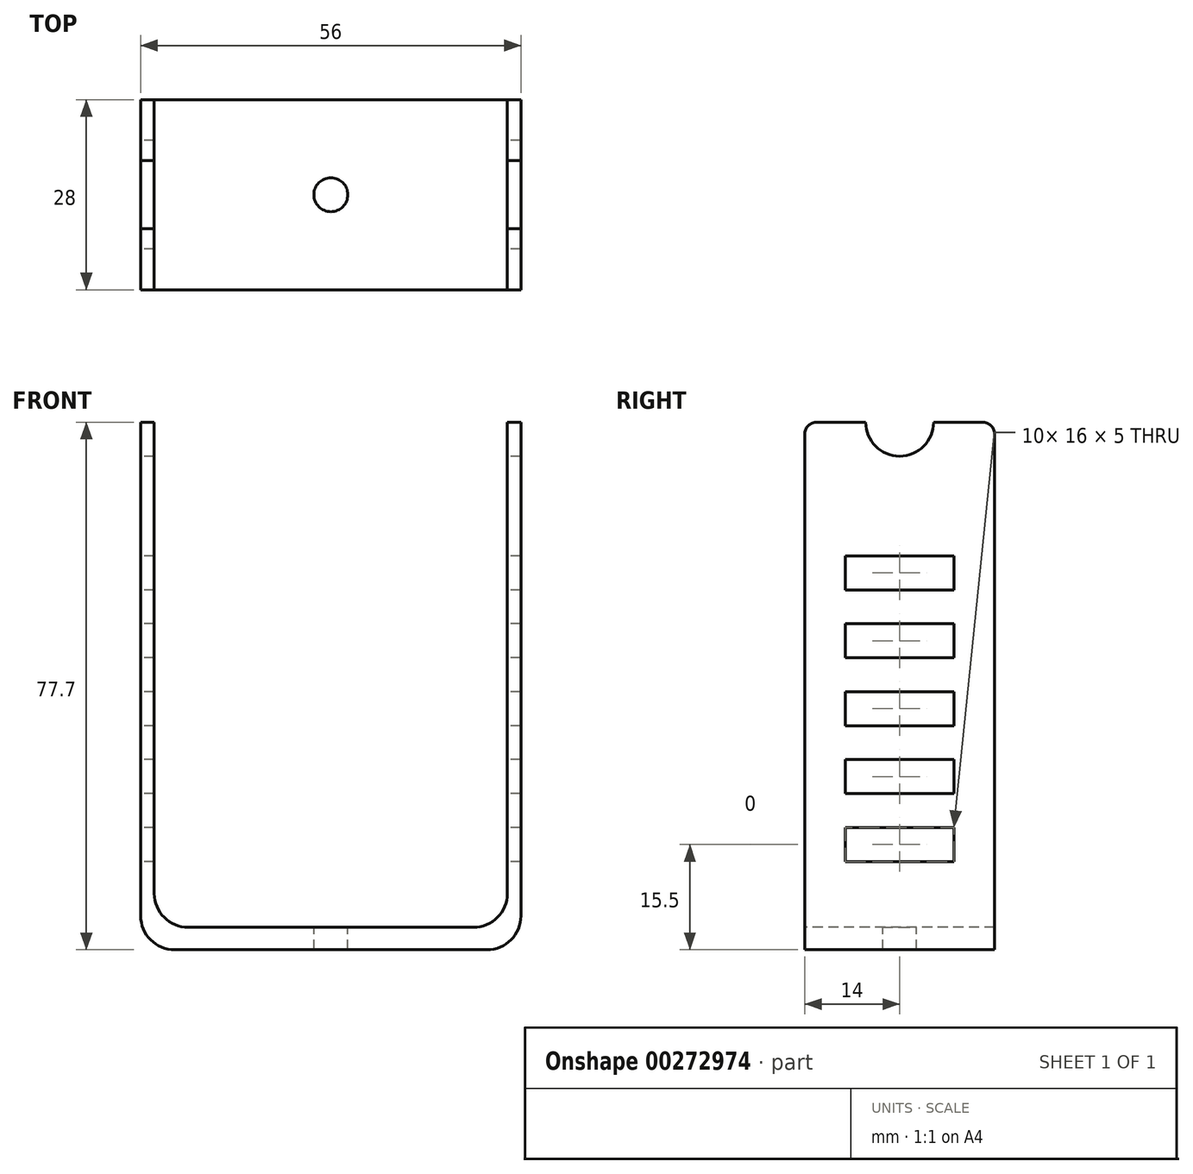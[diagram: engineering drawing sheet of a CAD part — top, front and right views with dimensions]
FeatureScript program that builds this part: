
annotation { "Feature Type Name" : "Feature", "Feature Type Description" : "" }
export const myFeature = defineFeature(function(context is Context, id is Id, definition is map)
    precondition{}
    {
        {
            var Q0;
            Q0=qCreatedBy(makeId("Right.planeOp"),FACE);
            var sketch = newSketch(context, id + "F0", { "sketchPlane" : qUnion([Q0])});
            skLineSegment(sketch, "E0.bottom", {"start": v(-14, 0) * mm, "end": v(14, 0) * mm});
            skLineSegment(sketch, "E0.top", {"start": v(-12.17, 77.7) * mm, "end": v(-5, 77.7) * mm});
            skLineSegment(sketch, "E0.left", {"start": v(-14, 0) * mm, "end": v(-14, 75.87) * mm});
            skLineSegment(sketch, "E0.right", {"start": v(14, 0) * mm, "end": v(14, 75.87) * mm});
            skLineSegment(sketch, "E1.bottom", {"start": v(-8, 18) * mm, "end": v(8, 18) * mm});
            skLineSegment(sketch, "E1.top", {"start": v(-8, 13) * mm, "end": v(8, 13) * mm});
            skLineSegment(sketch, "E1.left", {"start": v(-8, 18) * mm, "end": v(-8, 13) * mm});
            skLineSegment(sketch, "E1.right", {"start": v(8, 18) * mm, "end": v(8, 13) * mm});
            skLineSegment(sketch, "E2.0.1.0", {"start": v(-8, 23) * mm, "end": v(8, 23) * mm});
            skLineSegment(sketch, "E2.0.1.1", {"start": v(8, 28) * mm, "end": v(8, 23) * mm});
            skLineSegment(sketch, "E2.0.1.2", {"start": v(-8, 28) * mm, "end": v(8, 28) * mm});
            skLineSegment(sketch, "E2.0.1.3", {"start": v(-8, 28) * mm, "end": v(-8, 23) * mm});
            skLineSegment(sketch, "E2.0.2.0", {"start": v(-8, 33) * mm, "end": v(8, 33) * mm});
            skLineSegment(sketch, "E2.0.2.1", {"start": v(8, 38) * mm, "end": v(8, 33) * mm});
            skLineSegment(sketch, "E2.0.2.2", {"start": v(-8, 38) * mm, "end": v(8, 38) * mm});
            skLineSegment(sketch, "E2.0.2.3", {"start": v(-8, 38) * mm, "end": v(-8, 33) * mm});
            skLineSegment(sketch, "E2.0.3.0", {"start": v(-8, 43) * mm, "end": v(8, 43) * mm});
            skLineSegment(sketch, "E2.0.3.1", {"start": v(8, 48) * mm, "end": v(8, 43) * mm});
            skLineSegment(sketch, "E2.0.3.2", {"start": v(-8, 48) * mm, "end": v(8, 48) * mm});
            skLineSegment(sketch, "E2.0.3.3", {"start": v(-8, 48) * mm, "end": v(-8, 43) * mm});
            skLineSegment(sketch, "E2.0.4.0", {"start": v(-8, 53) * mm, "end": v(8, 53) * mm});
            skLineSegment(sketch, "E2.0.4.1", {"start": v(8, 58) * mm, "end": v(8, 53) * mm});
            skLineSegment(sketch, "E2.0.4.2", {"start": v(-8, 58) * mm, "end": v(8, 58) * mm});
            skLineSegment(sketch, "E2.0.4.3", {"start": v(-8, 58) * mm, "end": v(-8, 53) * mm});
            skLineSegment(sketch, "E2.direction1", {"start": v(-8, 13) * mm, "end": v(17, 13) * mm, "construction": true});
            skLineSegment(sketch, "E2.direction2", {"start": v(-8, 13) * mm, "end": v(-8, 23) * mm, "construction": true});
            skArc(sketch, "E3", {"start": v(-5, 77.7) * mm, "mid": v(0, 72.7) * mm, "end": v(5, 77.7) * mm});
            skLineSegment(sketch, "E4.trimOffspring", {"start": v(5, 77.7) * mm, "end": v(12.17, 77.7) * mm});
            skPoint(sketch, "E5.visualSharp", {"position": v(-14, 77.7) * mm});
            skArc(sketch, "E5.filletArc", {"start": v(-12.17, 77.7) * mm, "mid": v(-13.46, 77.16) * mm, "end": v(-14, 75.87) * mm});
            skPoint(sketch, "E6.visualSharp", {"position": v(14, 77.7) * mm});
            skArc(sketch, "E6.filletArc", {"start": v(14, 75.87) * mm, "mid": v(13.46, 77.16) * mm, "end": v(12.17, 77.7) * mm});
            skSolve(sketch);
        }
        {
            var Q0;
            Q0=makeQuery(id+"F0.imprint","IMPRINT",FACE,{"disambiguationData":[TD([[makeQuery(id+"F0.imprint","IMPRINT",EDGE,{"derivedFrom":sQuery(id+"F0.wireOp",EDGE,"E0.bottom")}),1.0]])]});
            extrude(context, id + "F1", {"entities" : qUnion([Q0]), "endBound" : BoundingType.SYMMETRIC, "depth" : 56 * mm});
        }
        {
            var Q0;
            Q0=makeQuery(id+"F1.opExtrude","SWEPT_FACE",FACE,{"disambiguationData":[OSD([sQuery(id+"F0.wireOp",EDGE,"E0.top")])]});
            var sketch = newSketch(context, id + "F2", { "sketchPlane" : qUnion([Q0])});
            skLineSegment(sketch, "E7.bottom", {"start": v(-26, 25.02) * mm, "end": v(26, 25.02) * mm});
            skLineSegment(sketch, "E7.top", {"start": v(-26, -24.24) * mm, "end": v(26, -24.24) * mm});
            skLineSegment(sketch, "E7.left", {"start": v(-26, 25.02) * mm, "end": v(-26, -24.24) * mm});
            skLineSegment(sketch, "E7.right", {"start": v(26, 25.02) * mm, "end": v(26, -24.24) * mm});
            skSolve(sketch);
        }
        {
            var Q0;
            Q0 = qSketchRegion(id + "F2", true);
            extrude(context, id + "F3", {"entities" : qUnion([Q0]), "operationType" : NewBodyOperationType.REMOVE, "oppositeDirection" : true, "depth" : (77.8 - 3.4) * mm});
        }
        {
            var Q0;
            Q0=makeQuery(id+"F1.opExtrude","CAP_EDGE",EDGE,{"disambiguationData":[OSD([sQuery(id+"F0.wireOp",EDGE,"E0.bottom")])],"isStart":true});
            var Q1;
            Q1=makeQuery(id+"F1.opExtrude","CAP_EDGE",EDGE,{"disambiguationData":[OSD([sQuery(id+"F0.wireOp",EDGE,"E0.bottom")])],"isStart":false});
            var Q2;
            Q2=makeQuery(id+"F3.boolean.opBoolean","COPY",EDGE,{"derivedFrom":makeQuery(id+"F3.opExtrude","CAP_EDGE",EDGE,{"disambiguationData":[OSD([sQuery(id+"F2.wireOp",EDGE,"E7.left")])],"isStart":false})});
            var Q3;
            Q3=makeQuery(id+"F3.boolean.opBoolean","COPY",EDGE,{"derivedFrom":makeQuery(id+"F3.opExtrude","CAP_EDGE",EDGE,{"disambiguationData":[OSD([sQuery(id+"F2.wireOp",EDGE,"E7.right")])],"isStart":false})});
            fillet(context, id + "F4", {"entities" : qUnion([Q0, Q1, Q2, Q3]), "radius" : 5 * mm, "tangentPropagation" : true, "allowEdgeOverflow" : false});
        }
        {
            var Q0;
            Q0=makeQuery(id+"F3.boolean.opBoolean","COPY",FACE,{"derivedFrom":makeQuery(id+"F3.opExtrude","CAP_FACE",FACE,{"disambiguationData":[OSD([sQuery(id+"F2.wireOp",EDGE,"E7.bottom"),sQuery(id+"F2.wireOp",EDGE,"E7.top"),sQuery(id+"F2.wireOp",EDGE,"E7.left"),sQuery(id+"F2.wireOp",EDGE,"E7.right")])],"isStart":false})});
            var sketch = newSketch(context, id + "F5", { "sketchPlane" : qUnion([Q0])});
            skCircle(sketch, "E8", {"center": v(0, 0) * mm, "radius": 2.5 * mm});
            skSolve(sketch);
        }
        {
            var Q0;
            Q0 = qSketchRegion(id + "F5", true);
            extrude(context, id + "F6", {"entities" : qUnion([Q0]), "operationType" : NewBodyOperationType.REMOVE, "endBound" : BoundingType.THROUGH_ALL, "oppositeDirection" : true, "depth" : 25 * mm});
        }
    });
